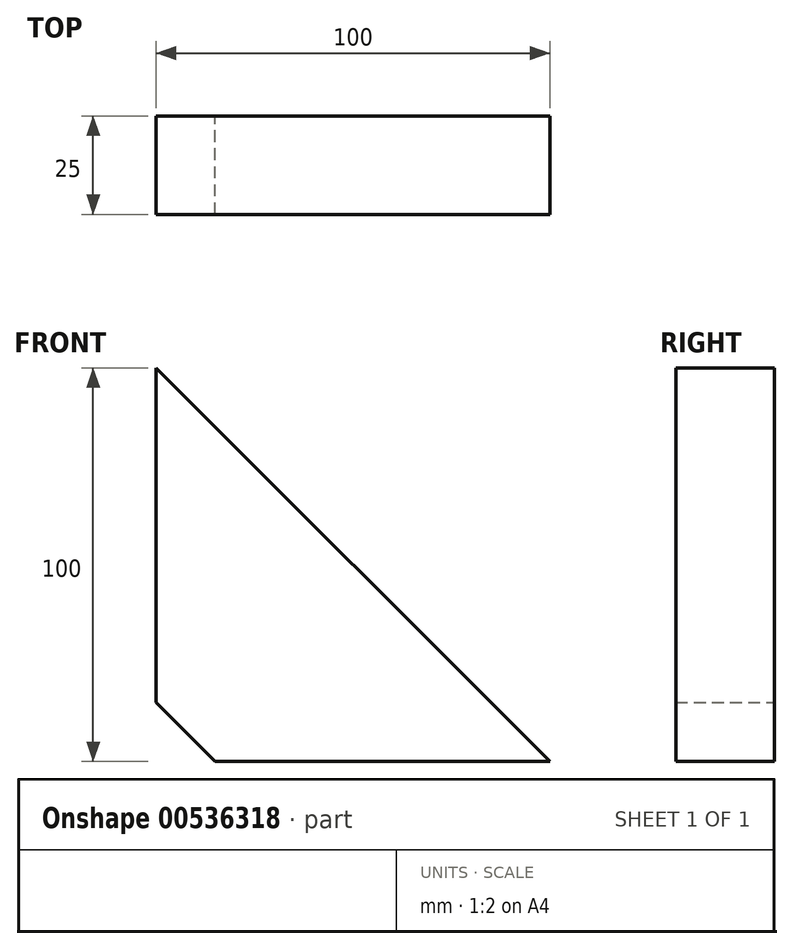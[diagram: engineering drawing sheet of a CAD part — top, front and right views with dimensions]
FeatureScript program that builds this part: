
annotation { "Feature Type Name" : "Feature", "Feature Type Description" : "" }
export const myFeature = defineFeature(function(context is Context, id is Id, definition is map)
    precondition{}
    {
        {
            var Q0;
            Q0=qCreatedBy(makeId("Front.planeOp"),FACE);
            var sketch = newSketch(context, id + "F0", { "sketchPlane" : qUnion([Q0])});
            skLineSegment(sketch, "E0.bottom", {"start": v(0, 0) * mm, "end": v(100, 0) * mm});
            skLineSegment(sketch, "E0.top", {"start": v(0, 100) * mm, "end": v(100, 100) * mm});
            skLineSegment(sketch, "E0.left", {"start": v(0, 0) * mm, "end": v(0, 100) * mm});
            skLineSegment(sketch, "E0.right", {"start": v(100, 0) * mm, "end": v(100, 100) * mm});
            skLineSegment(sketch, "E1", {"start": v(0, 100) * mm, "end": v(100, 0) * mm});
            skLineSegment(sketch, "E2", {"start": v(0, 15) * mm, "end": v(15, 0) * mm});
            skSolve(sketch);
        }
        {
            var Q0;
            {var subQ0=sQuery(id+"F0.wireOp",EDGE,"E1");Q0=makeQuery(id+"F0.imprint","IMPRINT",FACE,{"disambiguationData":[TD([[makeQuery(id+"F0.imprint","IMPRINT",EDGE,{"derivedFrom":subQ0}),-1.0]])]});}
            extrude(context, id + "F1", {"entities" : qUnion([Q0]), "depth" : 25 * mm, "offsetDistance" : 25 * mm});
        }
    });
